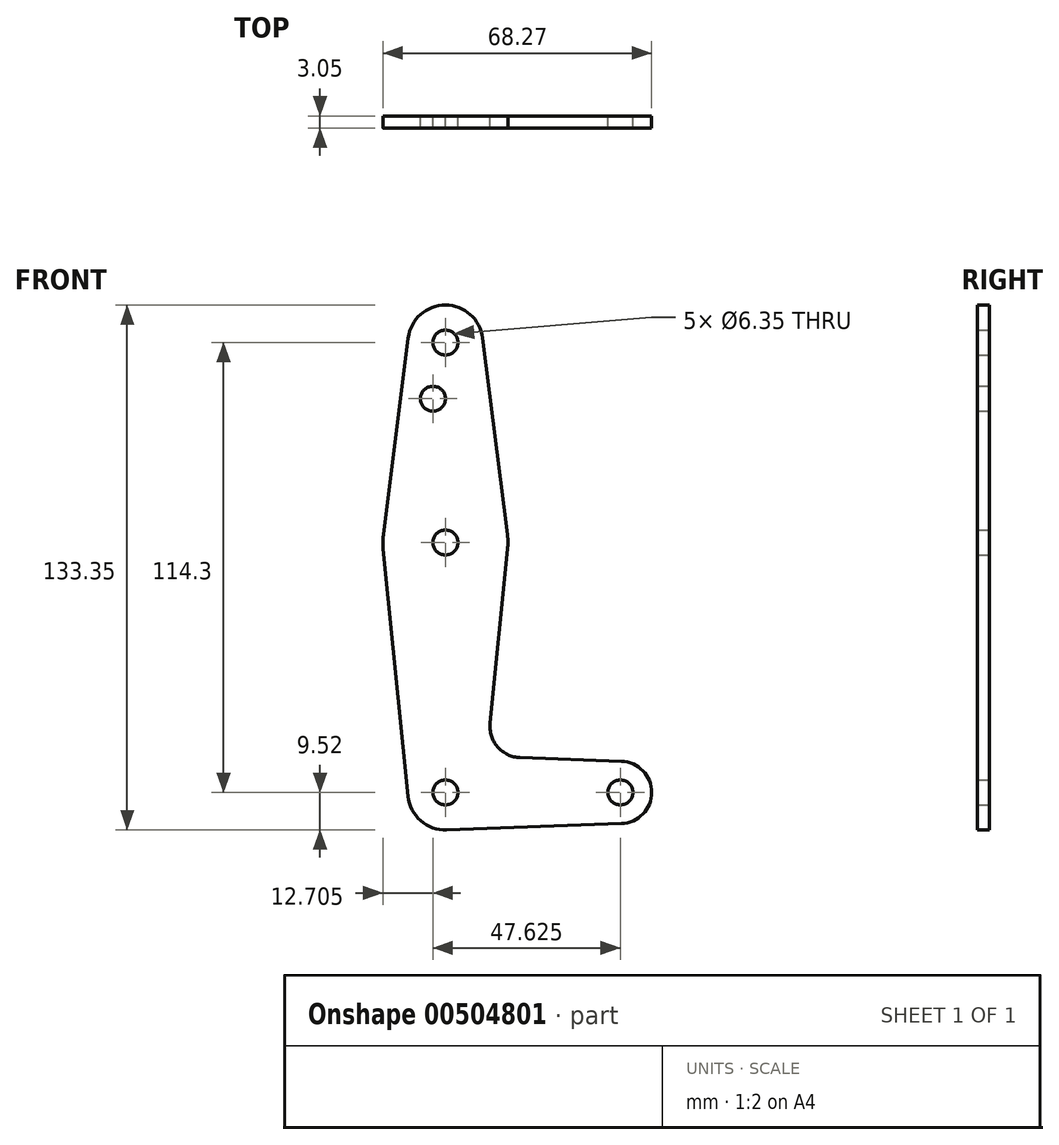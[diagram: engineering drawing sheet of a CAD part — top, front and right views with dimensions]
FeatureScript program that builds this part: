
annotation { "Feature Type Name" : "Feature", "Feature Type Description" : "" }
export const myFeature = defineFeature(function(context is Context, id is Id, definition is map)
    precondition{}
    {
        {
            var Q0;
            Q0=qCreatedBy(makeId("Front.planeOp"),FACE);
            var sketch = newSketch(context, id + "F0", { "sketchPlane" : qUnion([Q0])});
            skLineSegment(sketch, "E0", {"start": v(0, 114.3) * mm, "end": v(0, 0) * mm, "construction": true});
            skLineSegment(sketch, "E1", {"start": v(0, 0) * mm, "end": v(44.45, 0) * mm, "construction": true});
            skCircle(sketch, "E2", {"center": v(0, 114.3) * mm, "radius": 9.53 * mm});
            skCircle(sketch, "E3", {"center": v(44.45, 0) * mm, "radius": 7.94 * mm});
            skCircle(sketch, "E4", {"center": v(0, 0) * mm, "radius": 9.53 * mm});
            skCircle(sketch, "E5", {"center": v(0, 63.5) * mm, "radius": 15.88 * mm});
            skLineSegment(sketch, "E6", {"start": v(-15.75, 65.48) * mm, "end": v(-9.45, 115.5) * mm});
            skLineSegment(sketch, "E7", {"start": v(9.45, 115.5) * mm, "end": v(15.75, 65.48) * mm});
            skLineSegment(sketch, "E8", {"start": v(-15.8, 61.91) * mm, "end": v(-9.48, -0.95) * mm});
            skLineSegment(sketch, "E9", {"start": v(11.34, 17.6) * mm, "end": v(15.8, 61.91) * mm});
            skLineSegment(sketch, "E10", {"start": v(18.97, 8.85) * mm, "end": v(44.73, 7.93) * mm});
            skLineSegment(sketch, "E11", {"start": v(0.34, -9.52) * mm, "end": v(44.73, -7.93) * mm});
            skCircle(sketch, "E12", {"center": v(0, 114.3) * mm, "radius": 3.18 * mm});
            skCircle(sketch, "E13", {"center": v(0, 63.5) * mm, "radius": 3.18 * mm});
            skCircle(sketch, "E14", {"center": v(0, 0) * mm, "radius": 3.18 * mm});
            skCircle(sketch, "E15", {"center": v(44.45, 0) * mm, "radius": 3.18 * mm});
            skCircle(sketch, "E16", {"center": v(-3.17, 100.03) * mm, "radius": 3.18 * mm});
            skArc(sketch, "E17.filletArc", {"start": v(11.34, 17.6) * mm, "mid": v(13.26, 11.57) * mm, "end": v(18.97, 8.85) * mm});
            skSolve(sketch);
        }
        {
            var Q0;
            Q0 = qSketchRegion(id + "F0", true);
            extrude(context, id + "F1", {"entities" : qUnion([Q0]), "depth" : 3.05 * mm});
        }
    });
